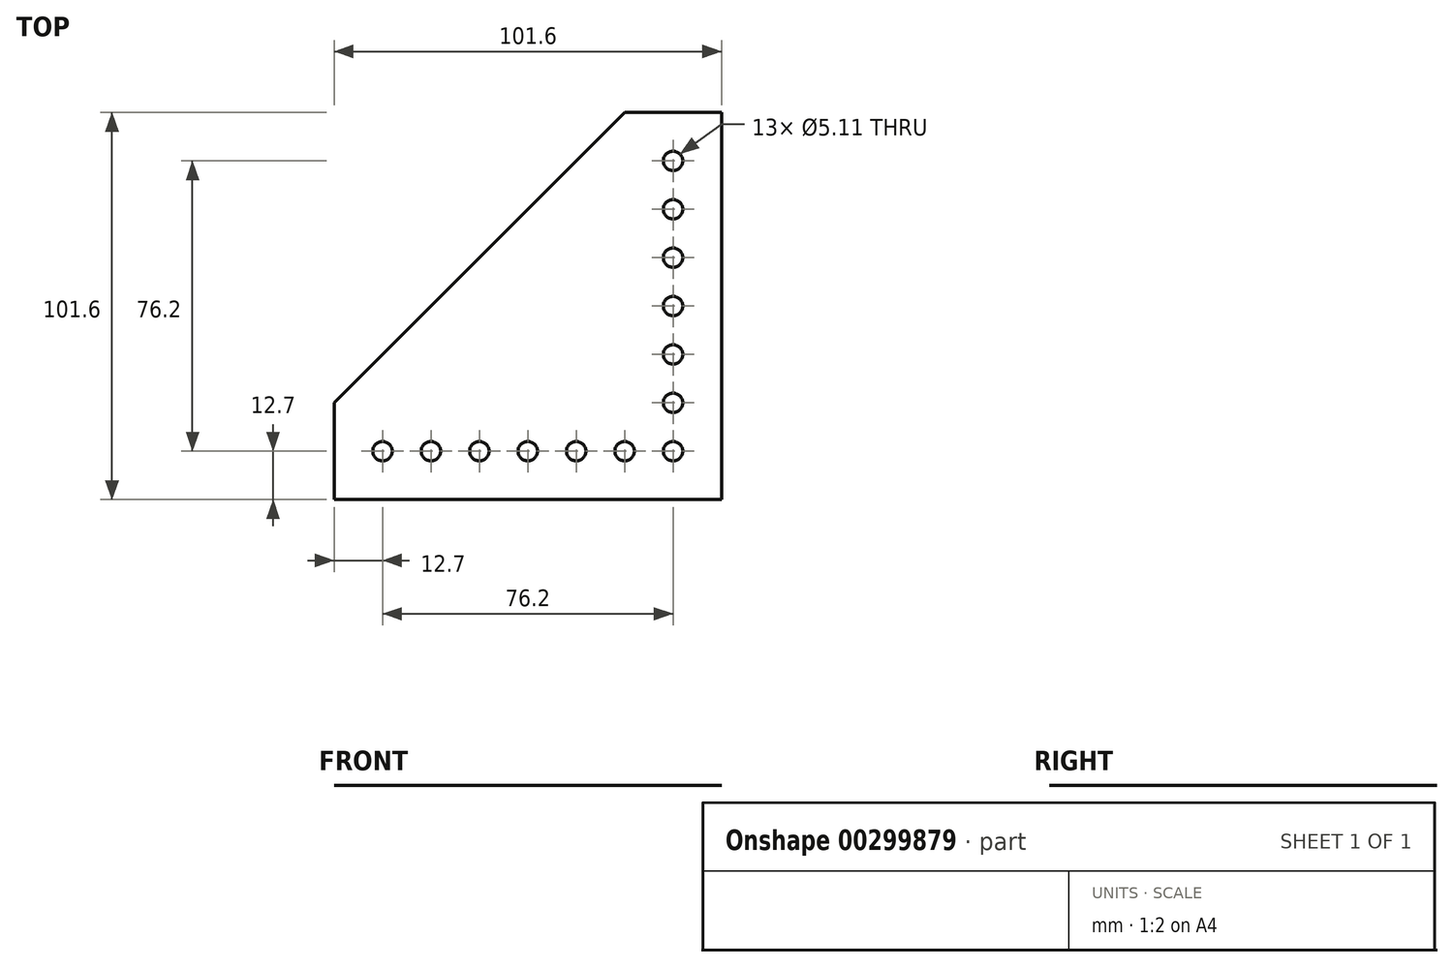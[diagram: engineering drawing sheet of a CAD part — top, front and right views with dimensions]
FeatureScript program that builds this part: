
annotation { "Feature Type Name" : "Feature", "Feature Type Description" : "" }
export const myFeature = defineFeature(function(context is Context, id is Id, definition is map)
    precondition{}
    {
        {
            var Q0;
            Q0=qCreatedBy(makeId("Top.planeOp"),FACE);
            var sketch = newSketch(context, id + "F0", { "sketchPlane" : qUnion([Q0])});
            skLineSegment(sketch, "E0", {"start": v(0, 0) * mm, "end": v(101.6, 0) * mm});
            skLineSegment(sketch, "E1", {"start": v(101.6, 0) * mm, "end": v(101.6, 101.6) * mm});
            skLineSegment(sketch, "E2", {"start": v(101.6, 101.6) * mm, "end": v(76.2, 101.6) * mm});
            skLineSegment(sketch, "E3", {"start": v(0, 0) * mm, "end": v(0, 25.4) * mm});
            skLineSegment(sketch, "E4", {"start": v(0, 25.4) * mm, "end": v(76.2, 25.4) * mm});
            skLineSegment(sketch, "E5", {"start": v(76.2, 25.4) * mm, "end": v(76.2, 101.6) * mm});
            skCircle(sketch, "E6", {"center": v(88.9, 88.9) * mm, "radius": 2.55 * mm});
            skPoint(sketch, "E6.centerSnap0", {"position": v(88.9, 101.6) * mm});
            skCircle(sketch, "E7.0.1.0", {"center": v(88.9, 76.2) * mm, "radius": 2.55 * mm});
            skLineSegment(sketch, "E7.direction1", {"start": v(88.9, 88.9) * mm, "end": v(114.3, 88.9) * mm, "construction": true});
            skLineSegment(sketch, "E7.direction2", {"start": v(88.9, 88.9) * mm, "end": v(88.9, 76.2) * mm, "construction": true});
            skCircle(sketch, "E8.0.0.2", {"center": v(88.9, 63.5) * mm, "radius": 2.55 * mm});
            skLineSegment(sketch, "E9.direction1", {"start": v(88.9, 63.5) * mm, "end": v(76.2, 63.5) * mm, "construction": true});
            skCircle(sketch, "E10.0.0.3", {"center": v(88.9, 50.8) * mm, "radius": 2.55 * mm});
            skCircle(sketch, "E10.0.0.4", {"center": v(88.9, 38.1) * mm, "radius": 2.55 * mm});
            skCircle(sketch, "E11.0.0.5", {"center": v(88.9, 25.4) * mm, "radius": 2.55 * mm});
            skCircle(sketch, "E11.0.0.6", {"center": v(88.9, 12.7) * mm, "radius": 2.55 * mm});
            skCircle(sketch, "E12.1.0.0", {"center": v(76.2, 12.7) * mm, "radius": 2.55 * mm});
            skCircle(sketch, "E12.2.0.0", {"center": v(63.5, 12.7) * mm, "radius": 2.55 * mm});
            skCircle(sketch, "E12.3.0.0", {"center": v(50.8, 12.7) * mm, "radius": 2.55 * mm});
            skCircle(sketch, "E12.4.0.0", {"center": v(38.1, 12.7) * mm, "radius": 2.55 * mm});
            skCircle(sketch, "E12.5.0.0", {"center": v(25.4, 12.7) * mm, "radius": 2.55 * mm});
            skCircle(sketch, "E12.6.0.0", {"center": v(12.7, 12.7) * mm, "radius": 2.55 * mm});
            skLineSegment(sketch, "E12.direction1", {"start": v(88.9, 12.7) * mm, "end": v(76.2, 12.7) * mm, "construction": true});
            skLineSegment(sketch, "E13", {"start": v(0, 25.4) * mm, "end": v(76.2, 101.6) * mm});
            skSolve(sketch);
        }
        {
            var Q0;
            Q0 = qSketchRegion(id + "F0", true);
            extrude(context, id + "F1", {"entities" : qUnion([Q0]), "depth" : 1 / 203.2 * mm});
        }
    });
